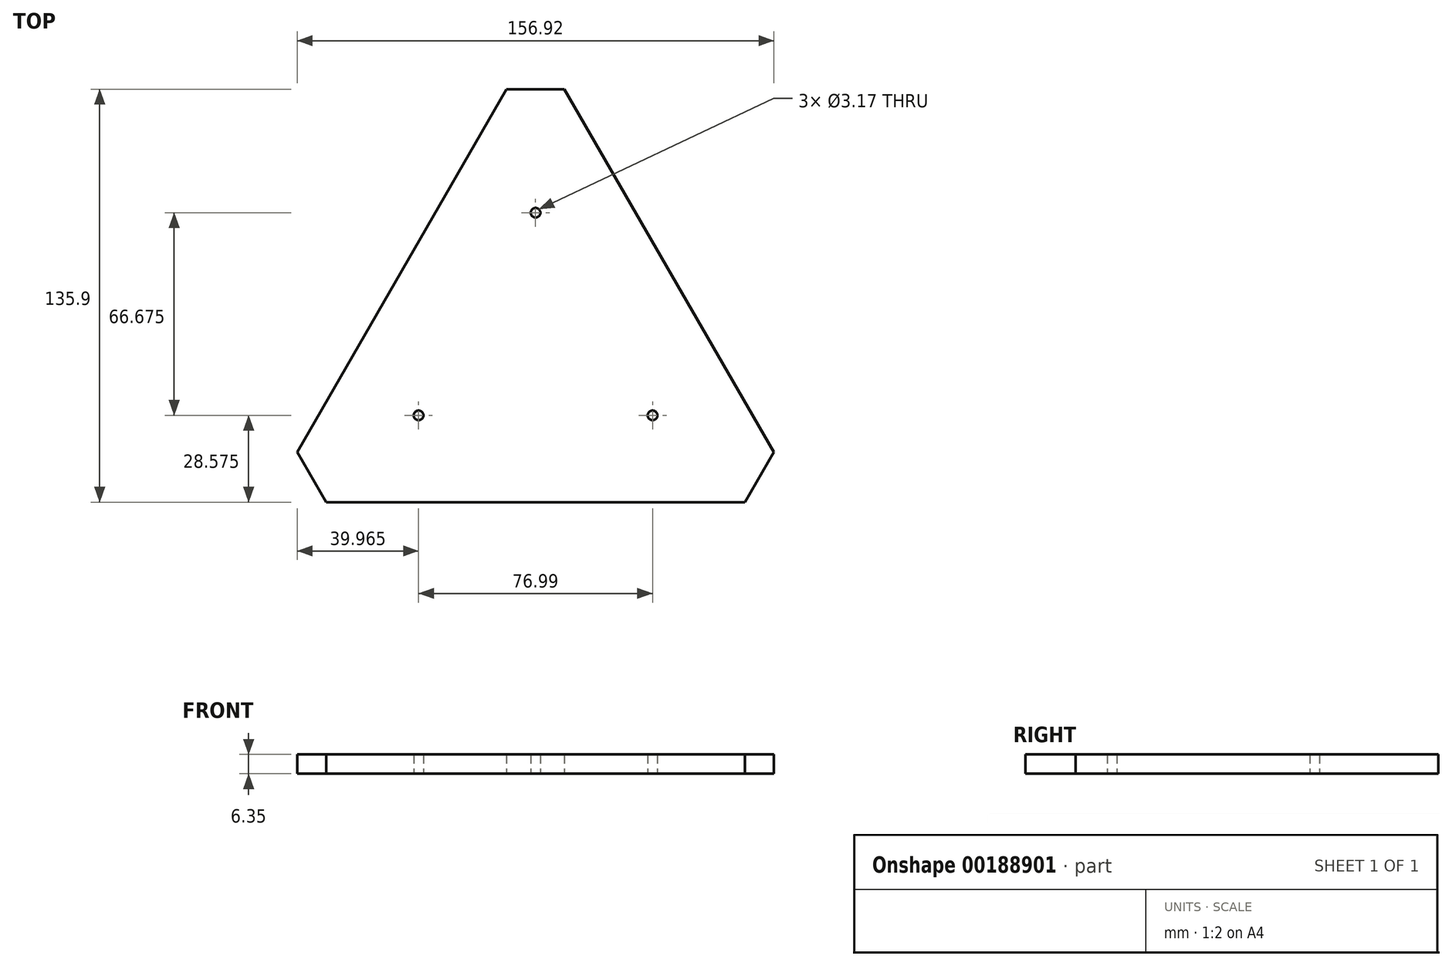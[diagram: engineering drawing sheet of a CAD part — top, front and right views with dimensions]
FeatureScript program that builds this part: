
annotation { "Feature Type Name" : "Feature", "Feature Type Description" : "" }
export const myFeature = defineFeature(function(context is Context, id is Id, definition is map)
    precondition{}
    {
        {
            var Q0;
            Q0=qCreatedBy(makeId("Top.planeOp"),FACE);
            var sketch = newSketch(context, id + "F0", { "sketchPlane" : qUnion([Q0])});
            skLineSegment(sketch, "E0", {"start": v(-9.53, 85.1) * mm, "end": v(9.52, 85.1) * mm});
            skLineSegment(sketch, "E1", {"start": v(9.52, 85.1) * mm, "end": v(78.46, -34.3) * mm});
            skLineSegment(sketch, "E2", {"start": v(78.46, -34.3) * mm, "end": v(68.94, -50.8) * mm});
            skLineSegment(sketch, "E3", {"start": v(68.94, -50.8) * mm, "end": v(-68.94, -50.8) * mm});
            skLineSegment(sketch, "E4", {"start": v(-68.94, -50.8) * mm, "end": v(-78.46, -34.3) * mm});
            skLineSegment(sketch, "E5", {"start": v(-78.46, -34.3) * mm, "end": v(-9.53, 85.1) * mm});
            skLineSegment(sketch, "E6", {"start": v(-73.7, -42.55) * mm, "end": v(0, 0) * mm, "construction": true});
            skLineSegment(sketch, "E7", {"start": v(0, 0) * mm, "end": v(73.7, -42.55) * mm, "construction": true});
            skLineSegment(sketch, "E8", {"start": v(0, 85.1) * mm, "end": v(0, 0) * mm, "construction": true});
            skLineSegment(sketch, "E9", {"start": v(-44, 25.4) * mm, "end": v(0, 0) * mm, "construction": true});
            skLineSegment(sketch, "E10", {"start": v(44, 25.4) * mm, "end": v(0, 0) * mm, "construction": true});
            skLineSegment(sketch, "E11", {"start": v(0, 0) * mm, "end": v(0, -50.8) * mm, "construction": true});
            skCircle(sketch, "E12", {"center": v(0, 0) * mm, "radius": 50.8 * mm, "construction": true});
            skCircle(sketch, "E13", {"center": v(0, 44.45) * mm, "radius": 1.59 * mm});
            skCircle(sketch, "E14", {"center": v(-38.5, -22.22) * mm, "radius": 1.59 * mm});
            skCircle(sketch, "E15", {"center": v(38.5, -22.22) * mm, "radius": 1.59 * mm});
            skLineSegment(sketch, "E16", {"start": v(-38.5, -22.22) * mm, "end": v(38.5, -22.22) * mm, "construction": true});
            skLineSegment(sketch, "E17", {"start": v(0, 44.45) * mm, "end": v(-38.5, -22.23) * mm, "construction": true});
            skLineSegment(sketch, "E18", {"start": v(38.5, -22.22) * mm, "end": v(0, 44.45) * mm, "construction": true});
            skSolve(sketch);
        }
        {
            var Q0;
            Q0=qSketchRegion(id+"F0",true);
            extrude(context, id + "F1", {"entities" : qUnion([Q0]), "depth" : 6.35 * mm});
        }
    });
